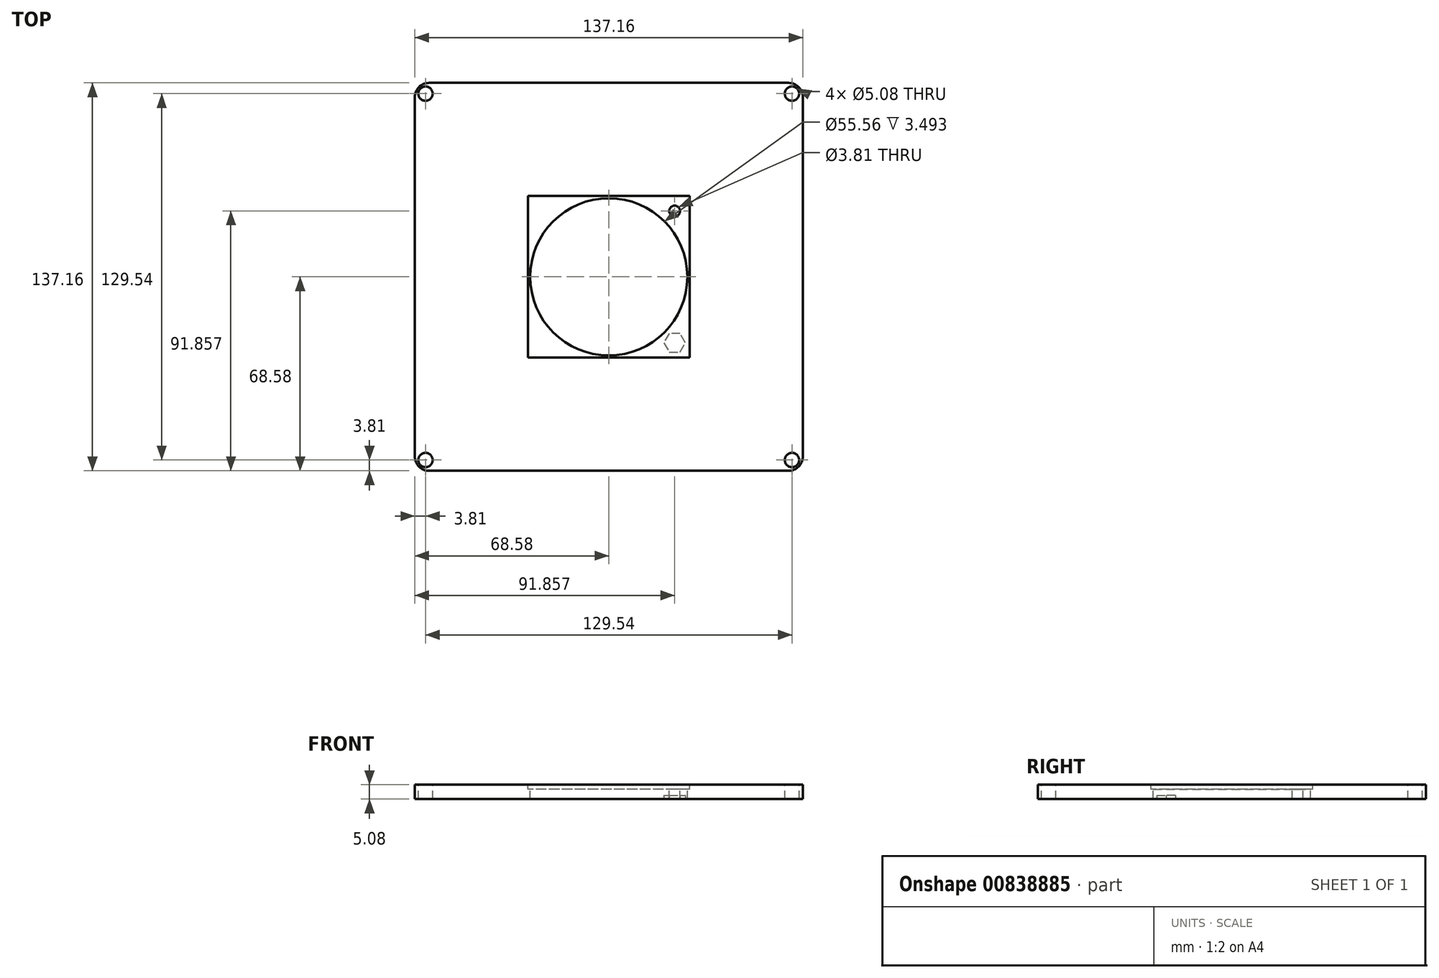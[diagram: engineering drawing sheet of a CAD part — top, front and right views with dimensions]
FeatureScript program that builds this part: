
annotation { "Feature Type Name" : "Feature", "Feature Type Description" : "" }
export const myFeature = defineFeature(function(context is Context, id is Id, definition is map)
    precondition{}
    {
        {
            var Q0;
            Q0=qCreatedBy(makeId("Top.planeOp"),FACE);
            var sketch = newSketch(context, id + "F0", { "sketchPlane" : qUnion([Q0])});
            skLineSegment(sketch, "E0.bottom", {"start": v(68.58, 68.58) * mm, "end": v(-68.58, 68.58) * mm});
            skLineSegment(sketch, "E0.top", {"start": v(68.58, -68.58) * mm, "end": v(-68.58, -68.58) * mm});
            skLineSegment(sketch, "E0.left", {"start": v(68.58, 68.58) * mm, "end": v(68.58, -68.58) * mm});
            skLineSegment(sketch, "E0.right", {"start": v(-68.58, 68.58) * mm, "end": v(-68.58, -68.58) * mm});
            skPoint(sketch, "E0.middle", {"position": v(0, 0) * mm});
            skSolve(sketch);
        }
        {
            var Q0;
            Q0=makeQuery(id+"F0.imprint","IMPRINT",FACE,{"disambiguationData":[TD([[makeQuery(id+"F0.imprint","IMPRINT",EDGE,{"derivedFrom":sQuery(id+"F0.wireOp",EDGE,"E0.bottom")}),1.0]])]});
            extrude(context, id + "F1", {"entities" : qUnion([Q0]), "depth" : 5.08 * mm, "offsetDistance" : 25.4 * mm});
        }
        {
            var Q0;
            Q0=makeQuery(id+"F1.opExtrude","SWEPT_EDGE",EDGE,{"disambiguationData":[OSD([sQuery(id+"F0.wireOp",EDGE,"E0.top"),sQuery(id+"F0.wireOp",EDGE,"E0.right")])]});
            var Q1;
            Q1=makeQuery(id+"F1.opExtrude","SWEPT_EDGE",EDGE,{"disambiguationData":[OSD([sQuery(id+"F0.wireOp",EDGE,"E0.top"),sQuery(id+"F0.wireOp",EDGE,"E0.left")])]});
            var Q2;
            Q2=makeQuery(id+"F1.opExtrude","SWEPT_EDGE",EDGE,{"disambiguationData":[OSD([sQuery(id+"F0.wireOp",EDGE,"E0.bottom"),sQuery(id+"F0.wireOp",EDGE,"E0.left")])]});
            var Q3;
            Q3=makeQuery(id+"F1.opExtrude","SWEPT_EDGE",EDGE,{"disambiguationData":[OSD([sQuery(id+"F0.wireOp",EDGE,"E0.bottom"),sQuery(id+"F0.wireOp",EDGE,"E0.right")])]});
            fillet(context, id + "F2", {"entities" : qUnion([Q0, Q1, Q2, Q3]), "radius" : 5.08 * mm, "tangentPropagation" : true, "allowEdgeOverflow" : false});
        }
        {
            var Q0;
            Q0=makeQuery(id+"F1.opExtrude","CAP_FACE",FACE,{"disambiguationData":[OSD([sQuery(id+"F0.wireOp",EDGE,"E0.bottom"),sQuery(id+"F0.wireOp",EDGE,"E0.top"),sQuery(id+"F0.wireOp",EDGE,"E0.left"),sQuery(id+"F0.wireOp",EDGE,"E0.right")])],"isStart":false});
            var sketch = newSketch(context, id + "F3", { "sketchPlane" : qUnion([Q0])});
            skCircle(sketch, "E1", {"center": v(0, 0) * mm, "radius": 27.78 * mm});
            skSolve(sketch);
        }
        {
            var Q0;
            Q0=qSketchRegion(id+"F3",true);
            var Q1;
            Q1=makeQuery(id+"F1.opExtrude","CAP_FACE",FACE,{"disambiguationData":[OSD([sQuery(id+"F0.wireOp",EDGE,"E0.bottom"),sQuery(id+"F0.wireOp",EDGE,"E0.top"),sQuery(id+"F0.wireOp",EDGE,"E0.left"),sQuery(id+"F0.wireOp",EDGE,"E0.right")])],"isStart":true});
            extrude(context, id + "F4", {"entities" : qUnion([Q0]), "operationType" : NewBodyOperationType.REMOVE, "endBound" : BoundingType.UP_TO_SURFACE, "oppositeDirection" : true, "depth" : 25.4 * mm, "endBoundEntityFace" : qUnion([Q1]), "offsetDistance" : 25.4 * mm});
        }
        {
            var Q0;
            Q0=makeQuery(id+"F1.opExtrude","CAP_FACE",FACE,{"disambiguationData":[OSD([sQuery(id+"F0.wireOp",EDGE,"E0.bottom"),sQuery(id+"F0.wireOp",EDGE,"E0.top"),sQuery(id+"F0.wireOp",EDGE,"E0.left"),sQuery(id+"F0.wireOp",EDGE,"E0.right")])],"isStart":false});
            var sketch = newSketch(context, id + "F5", { "sketchPlane" : qUnion([Q0])});
            skLineSegment(sketch, "E2.bottom", {"start": v(28.58, 28.58) * mm, "end": v(-28.57, 28.58) * mm});
            skLineSegment(sketch, "E2.top", {"start": v(28.57, -28.58) * mm, "end": v(-28.58, -28.58) * mm});
            skLineSegment(sketch, "E2.left", {"start": v(28.58, 28.58) * mm, "end": v(28.57, -28.58) * mm});
            skLineSegment(sketch, "E2.right", {"start": v(-28.57, 28.58) * mm, "end": v(-28.58, -28.58) * mm});
            skPoint(sketch, "E2.middle", {"position": v(0, 0) * mm});
            skSolve(sketch);
        }
        {
            var Q0;
            Q0=qSketchRegion(id+"F5",true);
            extrude(context, id + "F6", {"entities" : qUnion([Q0]), "operationType" : NewBodyOperationType.REMOVE, "oppositeDirection" : true, "depth" : 1.59 * mm, "offsetDistance" : 25.4 * mm});
        }
        {
            var Q0;
            Q0=makeQuery(id+"F6.boolean.opBoolean","COPY",FACE,{"derivedFrom":makeQuery(id+"F6.opExtrude","CAP_FACE",FACE,{"disambiguationData":[OSD([sQuery(id+"F5.wireOp",EDGE,"E2.bottom"),sQuery(id+"F5.wireOp",EDGE,"E2.top"),sQuery(id+"F5.wireOp",EDGE,"E2.left"),sQuery(id+"F5.wireOp",EDGE,"E2.right")])],"isStart":false})});
            var sketch = newSketch(context, id + "F7", { "sketchPlane" : qUnion([Q0])});
            skLineSegment(sketch, "E3", {"start": v(28.58, 28.58) * mm, "end": v(19.64, 19.64) * mm});
            skCircle(sketch, "E4", {"center": v(23.28, 23.28) * mm, "radius": 1.9 * mm});
            skSolve(sketch);
        }
        {
            var Q0;
            {var subQ0=sQuery(id+"F7.wireOp",EDGE,"E4");var subQ1=sQuery(id+"F7.wireOp",EDGE,"E3");var subQ2=makeQuery(id+"F7.imprint","INTERSECT",VERTEX,{"disambiguationData":[OD(0.0)],"derivedFrom":[subQ1,subQ0]});Q0=makeQuery(id+"F7.imprint","IMPRINT",FACE,{"disambiguationData":[TD([[makeQuery(id+"F7.imprint","IMPRINT",EDGE,{"disambiguationData":[TD([[subQ2,1.0]])],"derivedFrom":subQ1}),-1.0]])]});}
            var Q1;
            {var subQ0=sQuery(id+"F7.wireOp",EDGE,"E4");var subQ1=sQuery(id+"F7.wireOp",EDGE,"E3");var subQ2=makeQuery(id+"F7.imprint","INTERSECT",VERTEX,{"disambiguationData":[OD(0.0)],"derivedFrom":[subQ1,subQ0]});Q1=makeQuery(id+"F7.imprint","IMPRINT",FACE,{"disambiguationData":[TD([[makeQuery(id+"F7.imprint","IMPRINT",EDGE,{"disambiguationData":[TD([[subQ2,1.0]])],"derivedFrom":subQ1}),1.0]])]});}
            var Q2;
            Q2=makeQuery(id+"F1.opExtrude","CAP_FACE",FACE,{"disambiguationData":[OSD([sQuery(id+"F0.wireOp",EDGE,"E0.bottom"),sQuery(id+"F0.wireOp",EDGE,"E0.top"),sQuery(id+"F0.wireOp",EDGE,"E0.left"),sQuery(id+"F0.wireOp",EDGE,"E0.right")])],"isStart":true});
            extrude(context, id + "F8", {"entities" : qUnion([Q0, Q1]), "operationType" : NewBodyOperationType.REMOVE, "endBound" : BoundingType.UP_TO_SURFACE, "oppositeDirection" : true, "depth" : 25.4 * mm, "endBoundEntityFace" : qUnion([Q2]), "offsetDistance" : 25.4 * mm});
        }
        {
            var Q0;
            Q0=qCreatedBy(makeId("Front.planeOp"),FACE);
            var sketch = newSketch(context, id + "F9", { "sketchPlane" : qUnion([Q0])});
            skLineSegment(sketch, "E5", {"start": v(0, 79.43) * mm, "end": v(0, -44.4) * mm});
            skSolve(sketch);
        }
        {
            var Q0;
            Q0=makeQuery(id+"F1.opExtrude","CAP_FACE",FACE,{"disambiguationData":[OSD([sQuery(id+"F0.wireOp",EDGE,"E0.bottom"),sQuery(id+"F0.wireOp",EDGE,"E0.top"),sQuery(id+"F0.wireOp",EDGE,"E0.left"),sQuery(id+"F0.wireOp",EDGE,"E0.right")])],"isStart":true});
            var sketch = newSketch(context, id + "F10", { "sketchPlane" : qUnion([Q0])});
            skCircle(sketch, "E6.cCircle", {"center": v(23.28, 23.28) * mm, "radius": 3.3 * mm, "construction": true});
            skLineSegment(sketch, "E6.0", {"start": v(25.18, 26.58) * mm, "end": v(27.09, 23.28) * mm});
            skLineSegment(sketch, "E6.1", {"start": v(27.09, 23.28) * mm, "end": v(25.18, 19.98) * mm});
            skLineSegment(sketch, "E6.2", {"start": v(25.18, 19.98) * mm, "end": v(21.37, 19.98) * mm});
            skLineSegment(sketch, "E6.3", {"start": v(21.37, 19.98) * mm, "end": v(19.47, 23.28) * mm});
            skLineSegment(sketch, "E6.4", {"start": v(19.47, 23.28) * mm, "end": v(21.37, 26.58) * mm});
            skLineSegment(sketch, "E6.5", {"start": v(21.37, 26.58) * mm, "end": v(25.18, 26.58) * mm});
            skPoint(sketch, "E6.0.midPoint", {"position": v(26.13, 24.93) * mm});
            skSolve(sketch);
        }
        {
            var Q0;
            Q0=qSketchRegion(id+"F10",true);
            extrude(context, id + "F11", {"entities" : qUnion([Q0]), "operationType" : NewBodyOperationType.REMOVE, "oppositeDirection" : true, "depth" : 1.27 * mm, "offsetDistance" : 25.4 * mm});
        }
        {
            var Q0;
            Q0=makeQuery(id+"F1.opExtrude","CAP_FACE",FACE,{"disambiguationData":[OSD([sQuery(id+"F0.wireOp",EDGE,"E0.bottom"),sQuery(id+"F0.wireOp",EDGE,"E0.top"),sQuery(id+"F0.wireOp",EDGE,"E0.left"),sQuery(id+"F0.wireOp",EDGE,"E0.right")])],"isStart":false});
            var sketch = newSketch(context, id + "F12", { "sketchPlane" : qUnion([Q0])});
            skLineSegment(sketch, "E7.bottom", {"start": v(64.77, 64.77) * mm, "end": v(-64.77, 64.77) * mm});
            skLineSegment(sketch, "E7.top", {"start": v(64.77, -64.77) * mm, "end": v(-64.77, -64.77) * mm});
            skLineSegment(sketch, "E7.left", {"start": v(64.77, 64.77) * mm, "end": v(64.77, -64.77) * mm});
            skLineSegment(sketch, "E7.right", {"start": v(-64.77, 64.77) * mm, "end": v(-64.77, -64.77) * mm});
            skPoint(sketch, "E7.middle", {"position": v(0, 0) * mm});
            skCircle(sketch, "E8", {"center": v(-64.77, 64.77) * mm, "radius": 2.54 * mm});
            skCircle(sketch, "E9", {"center": v(64.77, 64.77) * mm, "radius": 2.54 * mm});
            skCircle(sketch, "E10", {"center": v(64.77, -64.77) * mm, "radius": 2.54 * mm});
            skCircle(sketch, "E11", {"center": v(-64.77, -64.77) * mm, "radius": 2.54 * mm});
            skSolve(sketch);
        }
        {
            var Q0;
            {var subQ0=sQuery(id+"F12.wireOp",EDGE,"E7.right");var subQ1=sQuery(id+"F12.wireOp",EDGE,"E7.bottom");var subQ2=makeQuery(id+"F12.imprint","INTERSECT",VERTEX,{"derivedFrom":[subQ1,subQ0]});Q0=makeQuery(id+"F12.imprint","IMPRINT",FACE,{"disambiguationData":[TD([[makeQuery(id+"F12.imprint","IMPRINT",EDGE,{"disambiguationData":[TD([[subQ2,1.0]])],"derivedFrom":subQ1}),-1.0]])]});}
            var Q1;
            {var subQ0=sQuery(id+"F12.wireOp",EDGE,"E7.right");var subQ1=sQuery(id+"F12.wireOp",EDGE,"E7.bottom");var subQ2=makeQuery(id+"F12.imprint","INTERSECT",VERTEX,{"derivedFrom":[subQ1,subQ0]});Q1=makeQuery(id+"F12.imprint","IMPRINT",FACE,{"disambiguationData":[TD([[makeQuery(id+"F12.imprint","IMPRINT",EDGE,{"disambiguationData":[TD([[subQ2,1.0]])],"derivedFrom":subQ1}),1.0]])]});}
            var Q2;
            {var subQ0=sQuery(id+"F12.wireOp",EDGE,"E7.right");var subQ1=sQuery(id+"F12.wireOp",EDGE,"E7.top");var subQ2=makeQuery(id+"F12.imprint","INTERSECT",VERTEX,{"derivedFrom":[subQ1,subQ0]});Q2=makeQuery(id+"F12.imprint","IMPRINT",FACE,{"disambiguationData":[TD([[makeQuery(id+"F12.imprint","IMPRINT",EDGE,{"disambiguationData":[TD([[subQ2,1.0]])],"derivedFrom":subQ1}),1.0]])]});}
            var Q3;
            {var subQ0=sQuery(id+"F12.wireOp",EDGE,"E7.right");var subQ1=sQuery(id+"F12.wireOp",EDGE,"E7.top");var subQ2=makeQuery(id+"F12.imprint","INTERSECT",VERTEX,{"derivedFrom":[subQ1,subQ0]});Q3=makeQuery(id+"F12.imprint","IMPRINT",FACE,{"disambiguationData":[TD([[makeQuery(id+"F12.imprint","IMPRINT",EDGE,{"disambiguationData":[TD([[subQ2,1.0]])],"derivedFrom":subQ1}),-1.0]])]});}
            var Q4;
            {var subQ0=sQuery(id+"F12.wireOp",EDGE,"E7.left");var subQ1=sQuery(id+"F12.wireOp",EDGE,"E7.top");var subQ2=makeQuery(id+"F12.imprint","INTERSECT",VERTEX,{"derivedFrom":[subQ1,subQ0]});Q4=makeQuery(id+"F12.imprint","IMPRINT",FACE,{"disambiguationData":[TD([[makeQuery(id+"F12.imprint","IMPRINT",EDGE,{"disambiguationData":[TD([[subQ2,-1.0]])],"derivedFrom":subQ1}),1.0]])]});}
            var Q5;
            {var subQ0=sQuery(id+"F12.wireOp",EDGE,"E7.left");var subQ1=sQuery(id+"F12.wireOp",EDGE,"E7.top");var subQ2=makeQuery(id+"F12.imprint","INTERSECT",VERTEX,{"derivedFrom":[subQ1,subQ0]});Q5=makeQuery(id+"F12.imprint","IMPRINT",FACE,{"disambiguationData":[TD([[makeQuery(id+"F12.imprint","IMPRINT",EDGE,{"disambiguationData":[TD([[subQ2,-1.0]])],"derivedFrom":subQ1}),-1.0]])]});}
            var Q6;
            {var subQ0=sQuery(id+"F12.wireOp",EDGE,"E7.left");var subQ1=sQuery(id+"F12.wireOp",EDGE,"E7.bottom");var subQ2=makeQuery(id+"F12.imprint","INTERSECT",VERTEX,{"derivedFrom":[subQ1,subQ0]});Q6=makeQuery(id+"F12.imprint","IMPRINT",FACE,{"disambiguationData":[TD([[makeQuery(id+"F12.imprint","IMPRINT",EDGE,{"disambiguationData":[TD([[subQ2,-1.0]])],"derivedFrom":subQ1}),1.0]])]});}
            var Q7;
            {var subQ0=sQuery(id+"F12.wireOp",EDGE,"E7.left");var subQ1=sQuery(id+"F12.wireOp",EDGE,"E7.bottom");var subQ2=makeQuery(id+"F12.imprint","INTERSECT",VERTEX,{"derivedFrom":[subQ1,subQ0]});Q7=makeQuery(id+"F12.imprint","IMPRINT",FACE,{"disambiguationData":[TD([[makeQuery(id+"F12.imprint","IMPRINT",EDGE,{"disambiguationData":[TD([[subQ2,-1.0]])],"derivedFrom":subQ1}),-1.0]])]});}
            var Q8;
            Q8=makeQuery(id+"F1.opExtrude","CAP_FACE",FACE,{"disambiguationData":[OSD([sQuery(id+"F0.wireOp",EDGE,"E0.bottom"),sQuery(id+"F0.wireOp",EDGE,"E0.top"),sQuery(id+"F0.wireOp",EDGE,"E0.left"),sQuery(id+"F0.wireOp",EDGE,"E0.right")])],"isStart":true});
            extrude(context, id + "F13", {"entities" : qUnion([Q0, Q1, Q2, Q3, Q4, Q5, Q6, Q7]), "operationType" : NewBodyOperationType.REMOVE, "endBound" : BoundingType.UP_TO_SURFACE, "oppositeDirection" : true, "depth" : 25.4 * mm, "endBoundEntityFace" : qUnion([Q8]), "offsetDistance" : 25.4 * mm});
        }
    });
